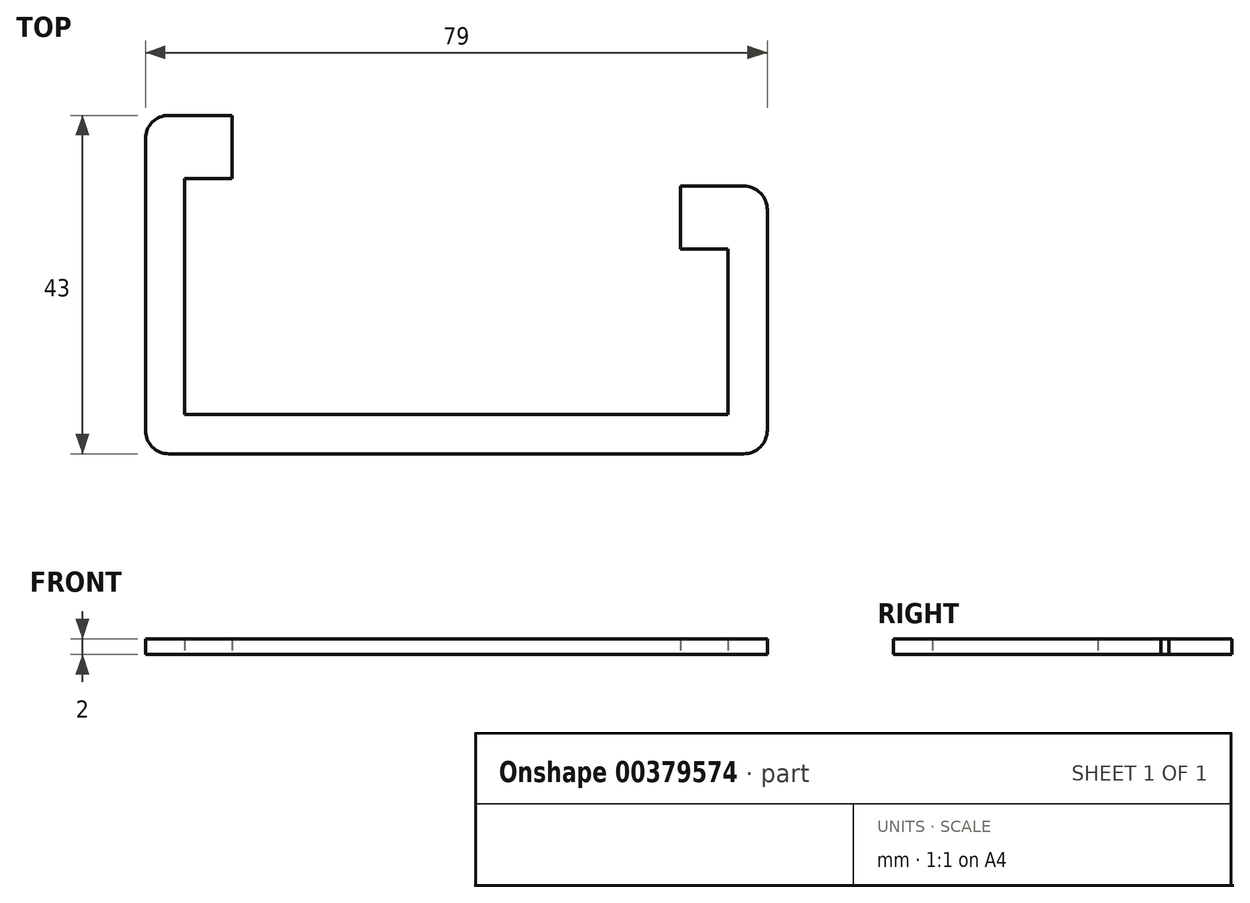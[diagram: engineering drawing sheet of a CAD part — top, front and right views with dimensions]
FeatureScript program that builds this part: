
annotation { "Feature Type Name" : "Feature", "Feature Type Description" : "" }
export const myFeature = defineFeature(function(context is Context, id is Id, definition is map)
    precondition{}
    {
        {
            var Q0;
            Q0=qCreatedBy(makeId("Top.planeOp"),FACE);
            var sketch = newSketch(context, id + "F0", { "sketchPlane" : qUnion([Q0])});
            skLineSegment(sketch, "E0", {"start": v(0, 0) * mm, "end": v(0, 43) * mm});
            skLineSegment(sketch, "E1", {"start": v(0, 43) * mm, "end": v(11, 43) * mm});
            skLineSegment(sketch, "E2", {"start": v(11, 43) * mm, "end": v(11, 35) * mm});
            skLineSegment(sketch, "E3", {"start": v(11, 35) * mm, "end": v(5, 35) * mm});
            skLineSegment(sketch, "E4", {"start": v(5, 35) * mm, "end": v(5, 5) * mm});
            skLineSegment(sketch, "E5", {"start": v(5, 5) * mm, "end": v(74, 5) * mm});
            skLineSegment(sketch, "E6", {"start": v(74, 5) * mm, "end": v(74, 26) * mm});
            skLineSegment(sketch, "E7", {"start": v(74, 26) * mm, "end": v(68, 26) * mm});
            skLineSegment(sketch, "E8", {"start": v(68, 26) * mm, "end": v(68, 34) * mm});
            skLineSegment(sketch, "E9", {"start": v(68, 34) * mm, "end": v(79, 34) * mm});
            skLineSegment(sketch, "E10", {"start": v(79, 34) * mm, "end": v(79, 0) * mm});
            skLineSegment(sketch, "E11", {"start": v(79, 0) * mm, "end": v(0, 0) * mm});
            skSolve(sketch);
        }
        {
            var Q0;
            Q0=makeQuery(id+"F0.imprint","IMPRINT",FACE,{"disambiguationData":[TD([[makeQuery(id+"F0.imprint","IMPRINT",EDGE,{"derivedFrom":sQuery(id+"F0.wireOp",EDGE,"E0")}),-1.0]])]});
            extrude(context, id + "F1", {"entities" : qUnion([Q0]), "depth" : 2 * mm, "offsetDistance" : 25 * mm});
        }
        {
            var Q0;
            Q0=makeQuery(id+"F1.opExtrude","SWEPT_EDGE",EDGE,{"disambiguationData":[OSD([sQuery(id+"F0.wireOp",EDGE,"E9"),sQuery(id+"F0.wireOp",EDGE,"E10")])]});
            var Q1;
            Q1=makeQuery(id+"F1.opExtrude","SWEPT_EDGE",EDGE,{"disambiguationData":[OSD([sQuery(id+"F0.wireOp",EDGE,"E10"),sQuery(id+"F0.wireOp",EDGE,"E11")])]});
            var Q2;
            Q2=makeQuery(id+"F1.opExtrude","SWEPT_EDGE",EDGE,{"disambiguationData":[OSD([sQuery(id+"F0.wireOp",EDGE,"E0"),sQuery(id+"F0.wireOp",EDGE,"E11")])]});
            var Q3;
            Q3=makeQuery(id+"F1.opExtrude","SWEPT_EDGE",EDGE,{"disambiguationData":[OSD([sQuery(id+"F0.wireOp",EDGE,"E0"),sQuery(id+"F0.wireOp",EDGE,"E1")])]});
            fillet(context, id + "F2", {"entities" : qUnion([Q0, Q1, Q2, Q3]), "radius" : 3 * mm, "tangentPropagation" : true, "allowEdgeOverflow" : false});
        }
    });
